# Revit family: DoorOpener_Garage_Liftmaster_Residential-JackShaft3800
name_source: partatom
category: Specialty Equipment
revit_build: Autodesk Revit 2016 (Build: 20150714_1515(x64)
units: mm (PartAtom-declared; Revit-internal decimal feet)

## family parameters
Always vertical = No
Cut with Voids When Loaded = No
Part Type = Normal
Room Calculation Point = No
Round Connector Dimension = Use Diameter
Shared = No
Work Plane-Based = Yes

## types (1)
- 3800
    Accent Material = Plastic - Liftmaster - Red
    Assembly Code = E1030900
    Construction Details = http://www.arcat.com
    Default Elevation = 4' - 0"
    Description = LiftMaster Jackshaft Residential Garage Door Operator - Model 3800
    Drive Type = Jackshaft
    Expected Lifespan (Years) = 0
    Green Building-LEED = http://www.arcat.com
    Has Battery Backup = Yes
    Installation-Fabrication = http://www.liftmaster.com
    Keynote = 08730
    Maintenance Schedule (Months) = 0
    Manufacturer = LiftMaster - The Chamberlain Group, Inc.
    Manufacturer Fax = 877-361-9589
    Manufacturer Website = http://www.liftmaster.com
    Material = Plastic - Liftmaster - Black
    Max Door Height = 14' - 0"
    Model = 3800
    Motor HP = 0
    Product Data = http://www.arcat.com
    Revision = R1_07-2011
    Sales Information = http://www.liftmaster.com
    Send Message = http://www.arcat.com
    Shaft Material = Metal - Steel - Liftmaster - Powder Coat - Black
    Specification = http://www.arcat.com
    URL = http://www.liftmaster.com
    Unit Depth = 0' - 6 7/8"
    Unit Height = 1' - 4 1/4"
    Unit Width = 0' - 6"
    Warranty Duration (Years) = 0

## geometry (parser evidence)
native form markers: Sweep x1
no freeform markers — native parametric forms only
